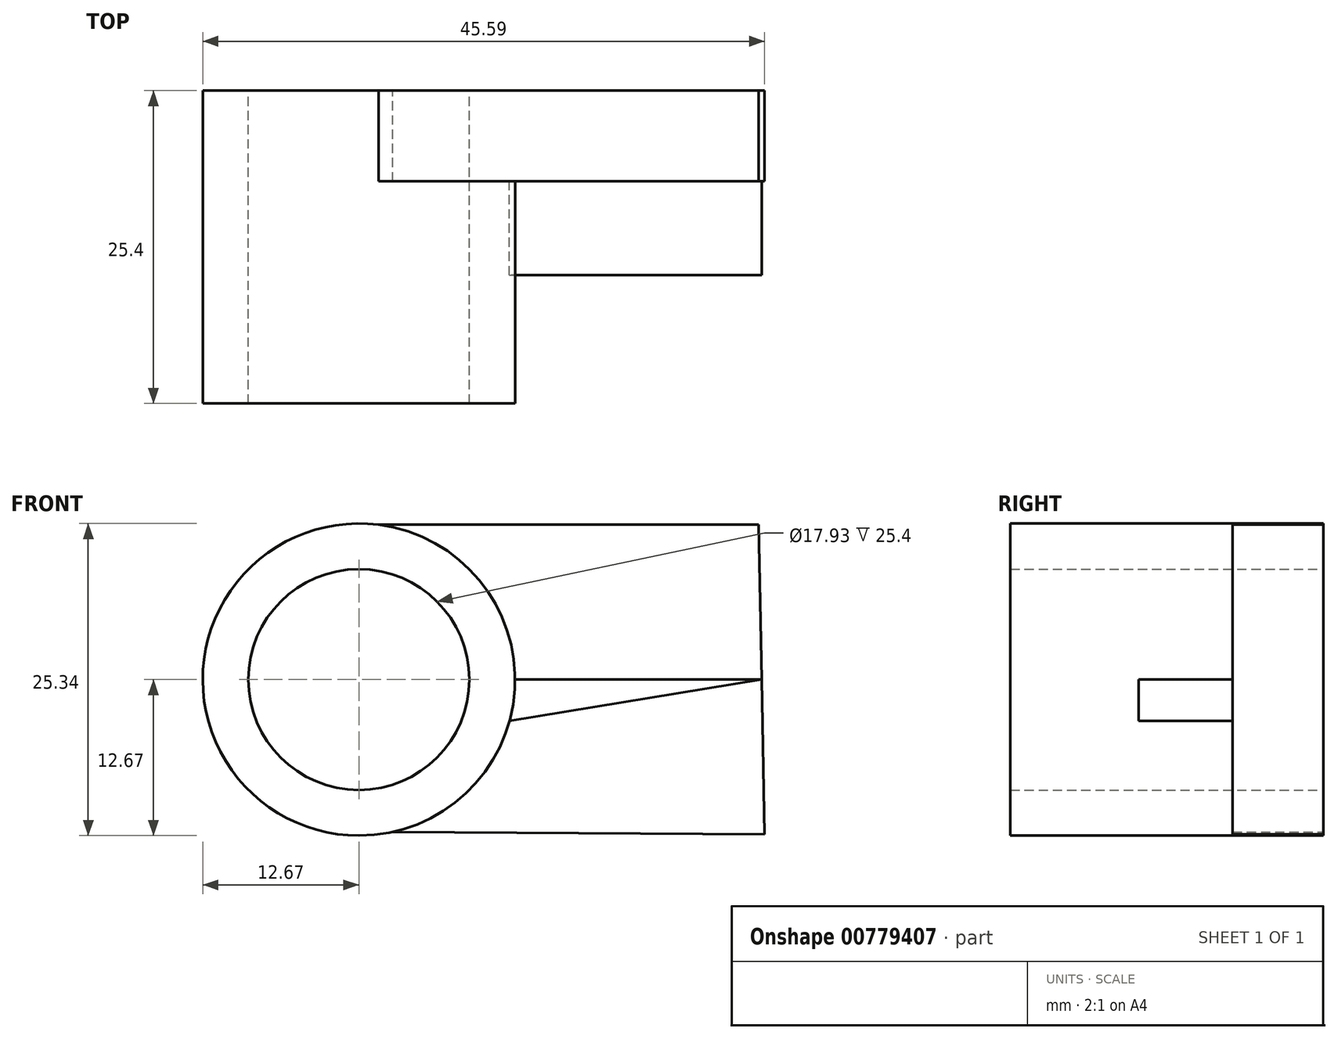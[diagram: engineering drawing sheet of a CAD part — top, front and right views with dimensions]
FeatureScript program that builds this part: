
annotation { "Feature Type Name" : "Feature", "Feature Type Description" : "" }
export const myFeature = defineFeature(function(context is Context, id is Id, definition is map)
    precondition{}
    {
        {
            var Q0;
            Q0=qCreatedBy(makeId("Front.planeOp"),FACE);
            var sketch = newSketch(context, id + "F0", { "sketchPlane" : qUnion([Q0])});
            skCircle(sketch, "E0", {"center": v(-12.67, 0) * mm, "radius": 12.67 * mm});
            skLineSegment(sketch, "E1", {"start": v(-11.08, 12.57) * mm, "end": v(19.76, 12.57) * mm});
            skLineSegment(sketch, "E2", {"start": v(19.76, 12.57) * mm, "end": v(20.25, -12.57) * mm});
            skLineSegment(sketch, "E3", {"start": v(20.25, -12.57) * mm, "end": v(-9.94, -12.37) * mm});
            skCircle(sketch, "E4", {"center": v(-12.67, 0) * mm, "radius": 8.96 * mm});
            skSolve(sketch);
        }
        {
            var Q0;
            Q0=makeQuery(id+"F0.imprint","IMPRINT",FACE,{"disambiguationData":[TD([[makeQuery(id+"F0.imprint","IMPRINT",EDGE,{"derivedFrom":sQuery(id+"F0.wireOp",EDGE,"E4")}),-1.0]])]});
            extrude(context, id + "F1", {"entities" : qUnion([Q0]), "depth" : 25.4 * mm, "offsetDistance" : 25.4 * mm});
        }
        {
            var Q0;
            {var subQ0=sQuery(id+"F0.wireOp",EDGE,"E1");Q0=makeQuery(id+"F0.imprint","IMPRINT",FACE,{"disambiguationData":[TD([[makeQuery(id+"F0.imprint","IMPRINT",EDGE,{"derivedFrom":subQ0}),-1.0]])]});}
            extrude(context, id + "F2", {"entities" : qUnion([Q0]), "operationType" : NewBodyOperationType.ADD, "depth" : 7.37 * mm, "offsetDistance" : 25.4 * mm});
        }
        {
            var Q0;
            Q0=makeQuery(id+"F2.opExtrude","CAP_FACE",FACE,{"disambiguationData":[OSD([sQuery(id+"F0.wireOp",EDGE,"E0"),sQuery(id+"F0.wireOp",EDGE,"E1"),sQuery(id+"F0.wireOp",EDGE,"E2"),sQuery(id+"F0.wireOp",EDGE,"E3")])],"isStart":false});
            var sketch = newSketch(context, id + "F3", { "sketchPlane" : qUnion([Q0])});
            skLineSegment(sketch, "E5", {"start": v(20, 0) * mm, "end": v(-49.26, -11.37) * mm});
            skLineSegment(sketch, "E6", {"start": v(-49.26, -11.37) * mm, "end": v(0, 0) * mm});
            skLineSegment(sketch, "E7", {"start": v(0, 0) * mm, "end": v(20, 0) * mm});
            skSolve(sketch);
        }
        {
            var Q0;
            {var subQ0=sQuery(id+"F3.wireOp",EDGE,"E7");Q0=makeQuery(id+"F3.imprint","IMPRINT",FACE,{"disambiguationData":[TD([[makeQuery(id+"F3.imprint","IMPRINT",EDGE,{"derivedFrom":subQ0}),-1.0]])]});}
            extrude(context, id + "F4", {"entities" : qUnion([Q0]), "operationType" : NewBodyOperationType.ADD, "depth" : 7.62 * mm, "offsetDistance" : 25.4 * mm});
        }
    });
